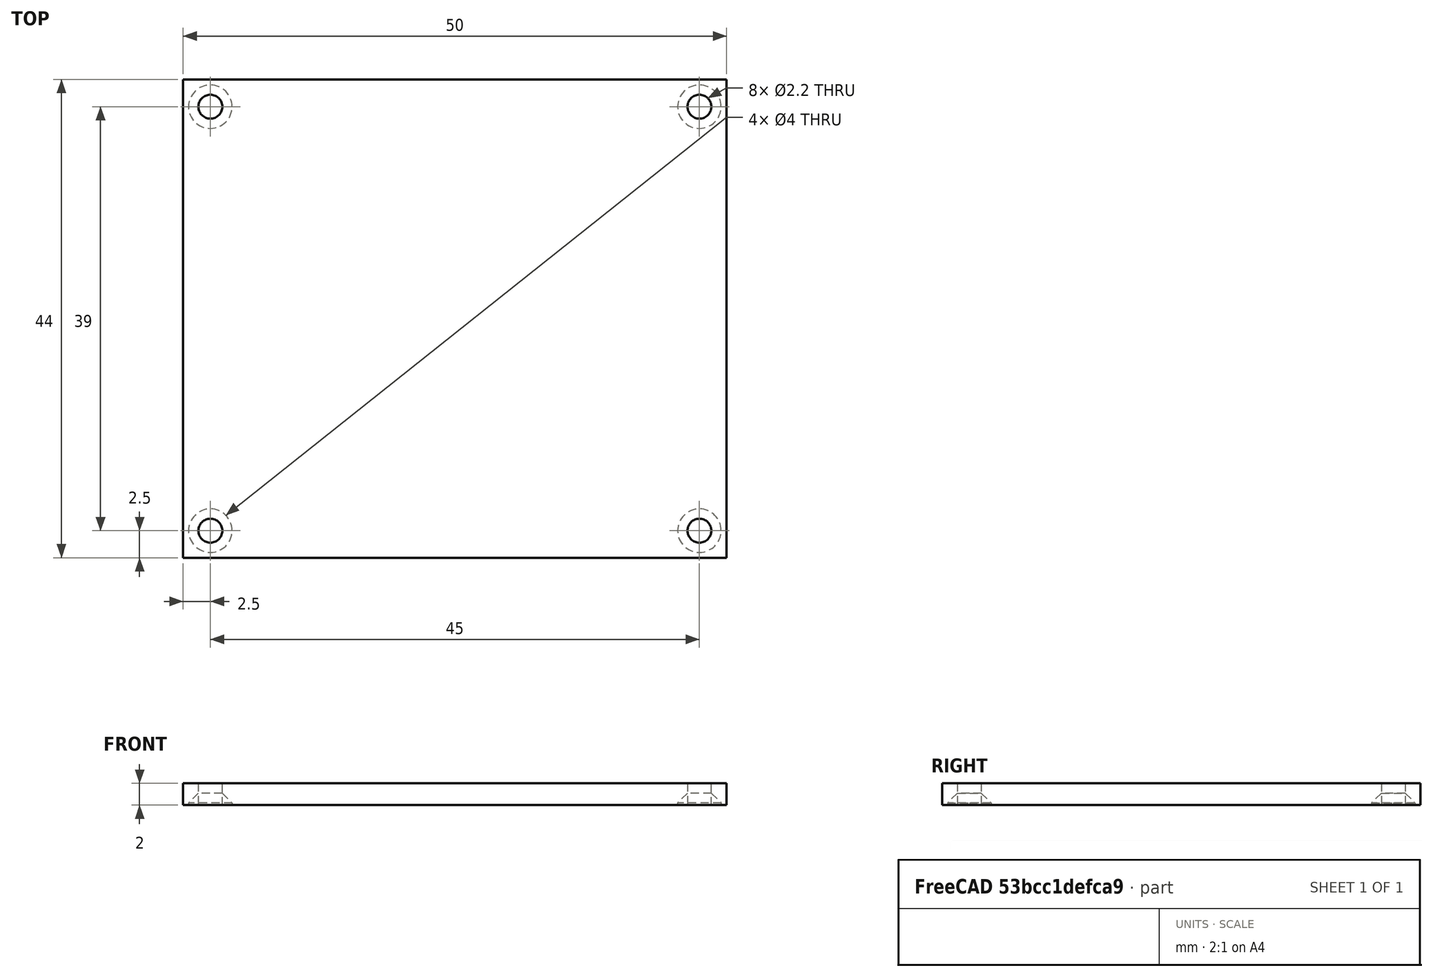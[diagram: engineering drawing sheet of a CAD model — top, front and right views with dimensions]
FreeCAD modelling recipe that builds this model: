
FCSTD DOCUMENT  (FreeCAD 0.19R24291 (Git))
Label: lid
License: All rights reserved
LicenseURL: http://en.wikipedia.org/wiki/All_rights_reserved
objects: TechDraw::DrawViewDimension×11, TechDraw::DrawProjGroupItem×3, Sketcher::SketchObject×2, PartDesign::Pad×1, PartDesign::Pocket×1, PartDesign::Body×1, Part::FeaturePython×1, TechDraw::DrawSVGTemplate×1, TechDraw::DrawProjGroup×1, TechDraw::DrawViewSection×1, TechDraw::DrawViewDetail×1, TechDraw::DrawPage×1
note: 8 computed .brp shape members not serialized (recipe doc carries the construction recipe); baked Part::Feature solids carry a one-line shape summary decoded from their .brp

FEATURE [Sketcher::SketchObject] Sketch
  FullyConstrained = true
  MapMode = 5
  Support = -> [XY_Plane]
  sketch-geometry (4):
    g0: LineSegment StartX=0 StartY=0 StartZ=0 EndX=50 EndY=0 EndZ=0
    g1: LineSegment StartX=50 StartY=0 StartZ=0 EndX=50 EndY=-44 EndZ=0
    g2: LineSegment StartX=50 StartY=-44 StartZ=0 EndX=0 EndY=-44 EndZ=0
    g3: LineSegment StartX=0 StartY=-44 StartZ=0 EndX=0 EndY=0 EndZ=0
  constraints (11):
    c: Coincident(g0,g1)
    c: Coincident(g1,g2)
    c: Coincident(g2,g3)
    c: Coincident(g3,g0)
    c: Horizontal(g0)
    c: Horizontal(g2)
    c: Vertical(g1)
    c: Vertical(g3)
    c: Coincident(g0,g-1)
    c: DistanceX(g2,g2) = 50
    c: DistanceY(g1,g1) = 44
FEATURE [PartDesign::Pad] Pad
  Direction = (1,1,1)
  Length = 2
  Length2 = 100
  Profile = -> Sketch
  Type = 0
FEATURE [Sketcher::SketchObject] Sketch001
  FullyConstrained = true
  MapMode = 5
  Support = -> [XY_Plane]
  sketch-geometry (4):
    g0: Circle CenterX=2.5 CenterY=-2.5 CenterZ=0 NormalX=0 NormalY=0 NormalZ=1 AngleXU=0 Radius=1.1
    g1: Circle CenterX=2.5 CenterY=-41.5 CenterZ=0 NormalX=0 NormalY=0 NormalZ=1 AngleXU=0 Radius=1.1
    g2: Circle CenterX=47.5 CenterY=-41.5 CenterZ=0 NormalX=0 NormalY=0 NormalZ=1 AngleXU=0 Radius=1.1
    g3: Circle CenterX=47.5 CenterY=-2.5 CenterZ=0 NormalX=0 NormalY=0 NormalZ=1 AngleXU=0 Radius=1.1
  constraints (12):
    c: Diameter(g0) = 2.2
    c: DistanceY(g0) = -2.5
    c: DistanceX(g0) = 2.5
    c: Diameter(g3) = 2.2
    c: Diameter(g2) = 2.2
    c: Diameter(g1) = 2.2
    c: DistanceY(g3) = -2.5
    c: DistanceX(g3) = 47.5
    c: DistanceX(g2) = 47.5
    c: DistanceY(g2) = -41.5
    c: DistanceY(g1) = -41.5
    c: DistanceX(g1) = 2.5
FEATURE [PartDesign::Pocket] Pocket
  BaseFeature = -> Pad
  Length = 2
  Length2 = 100
  Profile = -> Sketch001
  Reversed = true
  Type = 0
FEATURE [PartDesign::Body] Body
  Group = -> [Sketch,Pad,Sketch001,Pocket]
  Origin = -> Origin
  Tip = -> Pocket
FEATURE [Part::FeaturePython] Countersunk  # WARN: FeaturePython — macro-defined, semantics opaque (R4)
  baseObject = -> Pocket
  diameters = Edge12:M2:0:0:ISO14584 | Edge13:M2:0:0:ISO14584 | Edge14:M2:0:0:ISO14584 | Edge15:M2:0:0:ISO14584
FEATURE [TechDraw::DrawSVGTemplate] Template
  EditableTexts = Designed_by_Name=YXK; FC-Date=2021/9/6; FC-Title=Title; Subtitle=DiffAD620_lid
  Height = 210
  Orientation = 1
  Width = 297
FEATURE [TechDraw::DrawProjGroupItem] ProjItem  label="Front"
  CoarseView = false
  Direction = (0,0,-1)
  Focus = 100
  HardHidden = false
  IsoCount = 0
  IsoHidden = false
  IsoVisible = false
  LockPosition = true
  Perspective = false
  Rotation = 0
  RotationVector = (1,0,0)
  Scale = 1.5
  ScaleType = 2
  SeamHidden = false
  SeamVisible = true
  SmoothHidden = false
  SmoothVisible = true
  Source = -> [Countersunk]
  Type = 0
  X = 0
  XDirection = (1,0,0)
  Y = 0
FEATURE [TechDraw::DrawProjGroupItem] ProjItem001  label="FrontTopRight"
  CoarseView = false
  Direction = (0.57735,-0.57735,-0.57735)
  Focus = 100
  HardHidden = false
  IsoCount = 0
  IsoHidden = false
  IsoVisible = false
  LockPosition = false
  Perspective = false
  Rotation = 0
  RotationVector = (1,0,0)
  Scale = 1.5
  ScaleType = 2
  SeamHidden = false
  SeamVisible = true
  SmoothHidden = false
  SmoothVisible = true
  Source = -> [Countersunk]
  Type = 7
  X = -130.516
  XDirection = (0.707107,0,0.707107)
  Y = -73.2027
FEATURE [TechDraw::DrawProjGroupItem] ProjItem002  label="Left"
  CoarseView = false
  Direction = (-1,0,-1e-16)
  Focus = 100
  HardHidden = false
  IsoCount = 0
  IsoHidden = false
  IsoVisible = false
  LockPosition = false
  Perspective = false
  Rotation = 0
  RotationVector = (1,0,0)
  Scale = 1.5
  ScaleType = 2
  SeamHidden = false
  SeamVisible = true
  SmoothHidden = false
  SmoothVisible = true
  Source = -> [Countersunk]
  Type = 1
  X = 73.9135
  XDirection = (1e-16,0,-1)
  Y = 0
FEATURE [TechDraw::DrawProjGroup] ProjGroup
  Anchor = -> ProjItem
  AutoDistribute = false
  LockPosition = false
  ProjectionType = 0
  Rotation = 0
  Scale = 1.5
  ScaleType = 2
  Source = -> [Countersunk]
  Views = -> [ProjItem,ProjItem001,ProjItem002]
  X = 179.793
  Y = 137.026
  spacingX = 15
  spacingY = 15
FEATURE [TechDraw::DrawViewSection] SectionView  label="Section  - "
  BaseView = -> ProjItem
  CoarseView = false
  CutSurfaceDisplay = 2
  Direction = (1,0,0)
  FileGeomPattern = <path>
  FileHatchPattern = <path>
  Focus = 100
  FuseBeforeCut = false
  HardHidden = false
  HatchScale = 1
  IsoCount = 0
  IsoHidden = false
  IsoVisible = false
  LockPosition = false
  NameGeomPattern = Diamond
  Perspective = false
  Rotation = 0
  Scale = 1.5
  ScaleType = 0
  SeamHidden = false
  SeamVisible = true
  SectionDirection = 1
  SectionNormal = (1,0,0)
  SectionOrigin = (2.5,-22,1)
  SmoothHidden = false
  SmoothVisible = true
  Source = -> [Countersunk]
  X = 117.43
  XDirection = (0,0,1)
  Y = 135.891
FEATURE [TechDraw::DrawViewDetail] Detail  label="Detail 1"
  AnchorPoint = (0,20,0)
  BaseView = -> SectionView
  CoarseView = false
  Direction = (1,0,0)
  Focus = 100
  HardHidden = false
  IsoCount = 0
  IsoHidden = false
  IsoVisible = false
  LockPosition = false
  Perspective = false
  Radius = 4
  Reference = 1
  Rotation = 0
  Scale = 4.5
  ScaleType = 2
  SeamHidden = false
  SeamVisible = true
  SmoothHidden = false
  SmoothVisible = true
  Source = -> [Countersunk]
  X = 83.6652
  XDirection = (0,0,1)
  Y = 156.545
FEATURE [TechDraw::DrawViewDimension] Dimension
  Arbitrary = false
  ArbitraryTolerances = false
  EqualTolerance = true
  FormatSpec = %.0f
  FormatSpecOverTolerance = %+.2f
  FormatSpecUnderTolerance = %+.2f
  Inverted = false
  LockPosition = false
  MeasureType = 1
  OverTolerance = 0
  References2D = -> [ProjItem]
  Rotation = 0
  ScaleType = 0
  TheoreticalExact = false
  Type = 1
  UnderTolerance = 0
  X = 0.179598
  Y = -44.8534
FEATURE [TechDraw::DrawViewDimension] Dimension001
  Arbitrary = false
  ArbitraryTolerances = false
  EqualTolerance = true
  FormatSpec = %.0f
  FormatSpecOverTolerance = %+.2f
  FormatSpecUnderTolerance = %+.2f
  Inverted = false
  LockPosition = false
  MeasureType = 1
  OverTolerance = 0
  References2D = -> [ProjItem]
  Rotation = 0
  ScaleType = 0
  TheoreticalExact = false
  Type = 2
  UnderTolerance = 0
  X = 50.2514
  Y = 3.23276
FEATURE [TechDraw::DrawViewDimension] Dimension002
  Arbitrary = false
  ArbitraryTolerances = false
  EqualTolerance = true
  FormatSpec = %.0f
  FormatSpecOverTolerance = %+.2f
  FormatSpecUnderTolerance = %+.2f
  Inverted = false
  LockPosition = false
  MeasureType = 1
  OverTolerance = 0
  References2D = -> [ProjItem002]
  Rotation = 0
  ScaleType = 0
  TheoreticalExact = false
  Type = 1
  UnderTolerance = 0
  X = 15.0862
  Y = -44.8534
FEATURE [TechDraw::DrawViewDimension] Dimension003
  Arbitrary = false
  ArbitraryTolerances = false
  EqualTolerance = true
  FormatSpec = %.1f
  FormatSpecOverTolerance = %+.2f
  FormatSpecUnderTolerance = %+.2f
  Inverted = false
  LockPosition = false
  MeasureType = 1
  OverTolerance = 0
  References2D = -> [ProjItem]
  Rotation = 0
  ScaleType = 0
  TheoreticalExact = false
  Type = 1
  UnderTolerance = 0
  X = 24.8491
  Y = -37.5115
FEATURE [TechDraw::DrawViewDimension] Dimension004
  Arbitrary = false
  ArbitraryTolerances = false
  EqualTolerance = true
  FormatSpec = %.1f
  FormatSpecOverTolerance = %+.2f
  FormatSpecUnderTolerance = %+.2f
  Inverted = false
  LockPosition = false
  MeasureType = 1
  OverTolerance = 0
  References2D = -> [ProjItem]
  Rotation = 0
  ScaleType = 0
  TheoreticalExact = false
  Type = 2
  UnderTolerance = 0
  X = 43.7069
  Y = -17.6552
FEATURE [TechDraw::DrawViewDimension] Dimension005
  Arbitrary = false
  ArbitraryTolerances = false
  EqualTolerance = true
  FormatSpec = %.1f
  FormatSpecOverTolerance = %+.2f
  FormatSpecUnderTolerance = %+.2f
  Inverted = false
  LockPosition = false
  MeasureType = 1
  OverTolerance = 0
  References2D = -> [Detail]
  Rotation = 0
  ScaleType = 0
  TheoreticalExact = false
  Type = 1
  UnderTolerance = 0
  X = 14.6876
  Y = 34.4888
FEATURE [TechDraw::DrawViewDimension] Dimension006
  Arbitrary = false
  ArbitraryTolerances = false
  EqualTolerance = true
  FormatSpec = %.1f
  FormatSpecOverTolerance = %+.2f
  FormatSpecUnderTolerance = %+.2f
  Inverted = false
  LockPosition = false
  MeasureType = 1
  OverTolerance = 0
  References2D = -> [Detail]
  Rotation = 0
  ScaleType = 0
  TheoreticalExact = false
  Type = 1
  UnderTolerance = 0
  X = -9.9273
  Y = 25.9649
FEATURE [TechDraw::DrawViewDimension] Dimension007
  Arbitrary = false
  ArbitraryTolerances = false
  EqualTolerance = true
  FormatSpec = %.1f
  FormatSpecOverTolerance = %+.2f
  FormatSpecUnderTolerance = %+.2f
  Inverted = false
  LockPosition = false
  MeasureType = 1
  OverTolerance = 0
  References2D = -> [Detail]
  Rotation = 0
  ScaleType = 0
  TheoreticalExact = false
  Type = 2
  UnderTolerance = 0
  X = 8.98994
  Y = -0.454023
FEATURE [TechDraw::DrawViewDimension] Dimension009
  Arbitrary = false
  ArbitraryTolerances = false
  EqualTolerance = true
  FormatSpec = %.1f
  FormatSpecOverTolerance = %+.2f
  FormatSpecUnderTolerance = %+.2f
  Inverted = false
  LockPosition = false
  MeasureType = 1
  OverTolerance = 0
  References2D = -> [Detail]
  Rotation = 0
  ScaleType = 0
  TheoreticalExact = false
  Type = 1
  UnderTolerance = 0
  X = 1.69713
  Y = -20.9483
FEATURE [TechDraw::DrawViewDimension] Dimension010
  Arbitrary = false
  ArbitraryTolerances = false
  EqualTolerance = true
  FormatSpec = %.0f
  FormatSpecOverTolerance = %+.2f
  FormatSpecUnderTolerance = %+.2f
  Inverted = false
  LockPosition = false
  MeasureType = 1
  OverTolerance = 0
  References2D = -> [Detail]
  Rotation = 0
  ScaleType = 0
  TheoreticalExact = false
  Type = 6
  UnderTolerance = 0
  X = -35.3788
  Y = 0.718393
FEATURE [TechDraw::DrawViewDimension] Dimension011
  Arbitrary = false
  ArbitraryTolerances = false
  EqualTolerance = true
  FormatSpec = %.2f
  FormatSpecOverTolerance = %+.2f
  FormatSpecUnderTolerance = %+.2f
  Inverted = false
  LockPosition = false
  MeasureType = 1
  OverTolerance = 0
  References2D = -> [Detail]
  Rotation = 0
  ScaleType = 0
  TheoreticalExact = false
  Type = 2
  UnderTolerance = 0
  X = -11.839
  Y = -2.07836
FEATURE [TechDraw::DrawPage] Page
  KeepUpdated = true
  NextBalloonIndex = 1
  ProjectionType = 0
  Template = -> Template
  Views = -> [ProjGroup,SectionView,Detail,Dimension,Dimension001,Dimension002,Dimension003,Dimension004,Dimension005,Dimension006,Dimension007,Dimension009,Dimension010,Dimension011]
note: 2 file-system paths scrubbed to <path> (originals preserved in the JSON sidecar)
